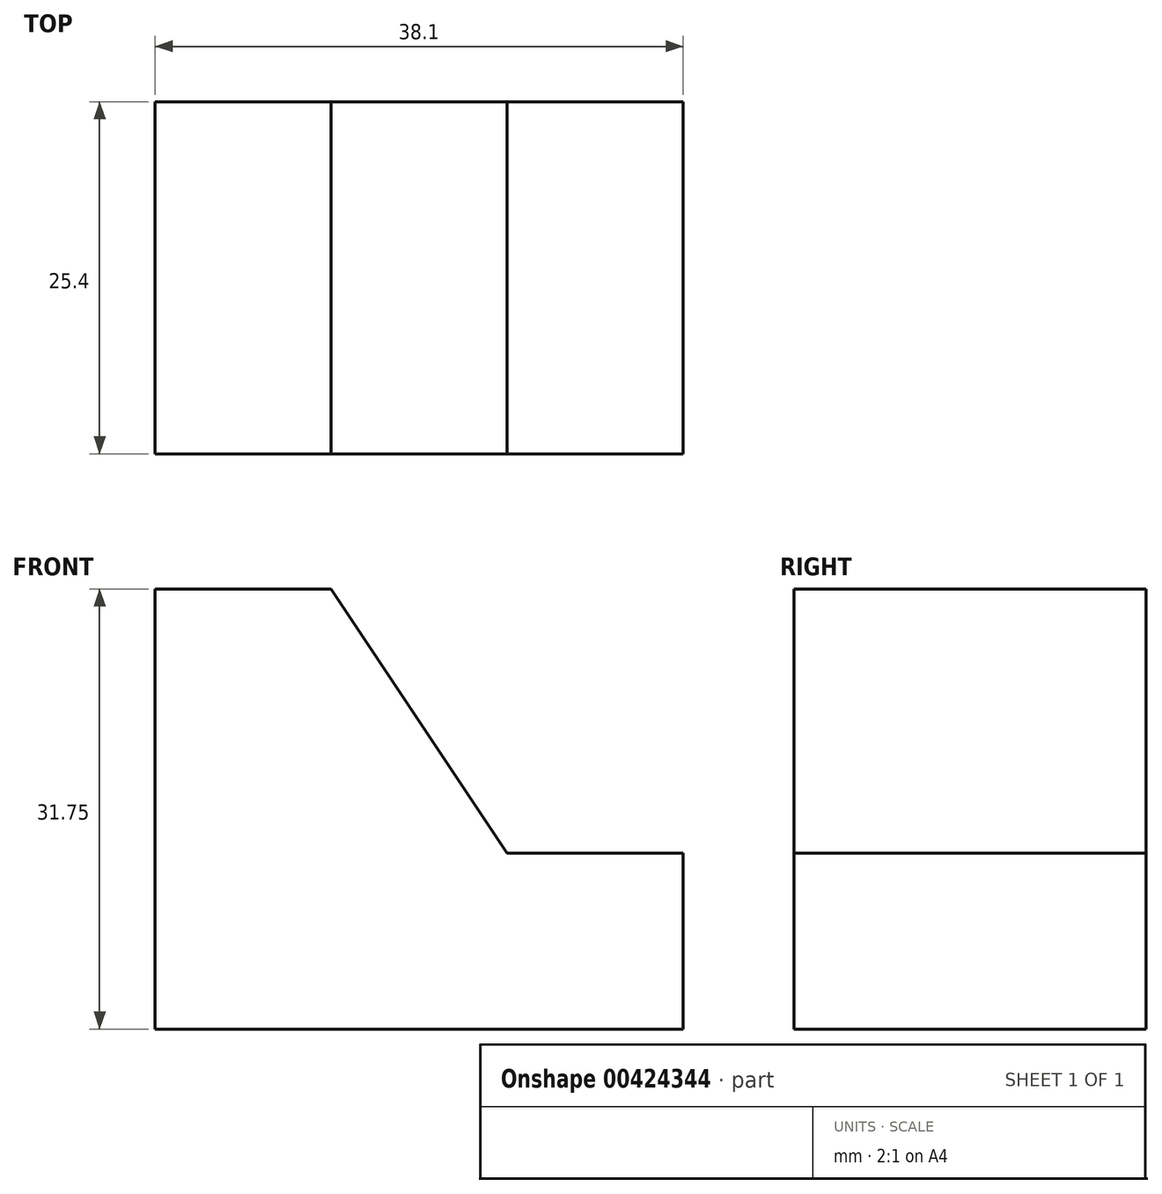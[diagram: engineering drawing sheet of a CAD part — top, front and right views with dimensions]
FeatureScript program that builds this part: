
annotation { "Feature Type Name" : "Feature", "Feature Type Description" : "" }
export const myFeature = defineFeature(function(context is Context, id is Id, definition is map)
    precondition{}
    {
        {
            var Q0;
            Q0=qCreatedBy(makeId("Front.planeOp"),FACE);
            var sketch = newSketch(context, id + "F0", { "sketchPlane" : qUnion([Q0])});
            skLineSegment(sketch, "E0", {"start": v(0, 0) * mm, "end": v(38.1, 0) * mm});
            skLineSegment(sketch, "E1", {"start": v(38.1, 0) * mm, "end": v(38.1, 12.7) * mm});
            skLineSegment(sketch, "E2", {"start": v(38.1, 12.7) * mm, "end": v(25.4, 12.7) * mm});
            skLineSegment(sketch, "E3", {"start": v(0, 0) * mm, "end": v(0, 31.75) * mm});
            skLineSegment(sketch, "E4", {"start": v(0, 31.75) * mm, "end": v(12.7, 31.75) * mm});
            skLineSegment(sketch, "E5", {"start": v(12.7, 31.75) * mm, "end": v(25.4, 12.7) * mm});
            skSolve(sketch);
        }
        {
            var Q0;
            Q0=makeQuery(id+"F0.imprint","IMPRINT",FACE,{"disambiguationData":[TD([[makeQuery(id+"F0.imprint","IMPRINT",EDGE,{"derivedFrom":sQuery(id+"F0.wireOp",EDGE,"E0")}),1.0]])]});
            extrude(context, id + "F1", {"entities" : qUnion([Q0]), "depth" : 25.4 * mm});
        }
    });
